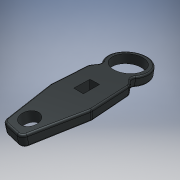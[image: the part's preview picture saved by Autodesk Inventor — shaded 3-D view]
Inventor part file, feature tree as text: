
AUTODESK INVENTOR PART (.ipt)
format: ipt  version: 2018 (Build 220112000, 112)  size: 219,648 bytes
history: native  units: mm
features: fillet x2, other x1, extrude x1, sketch x1
ambient origin geometry x8: Origin, YZ Plane, XZ Plane, XY Plane, X Axis, Y Axis, Z Axis, Center Point
bodies: Body1 (feature_tree)
feature tree (5):
  other  "Těleso1"
  extrude  "Vysunutí1"  Depth=3.0mm
  fillet  "Zaoblení1"  Radius=6.0mm
  fillet  "Zaoblení2"  Radius=1.0mm
  sketch  "Náčrt1"
